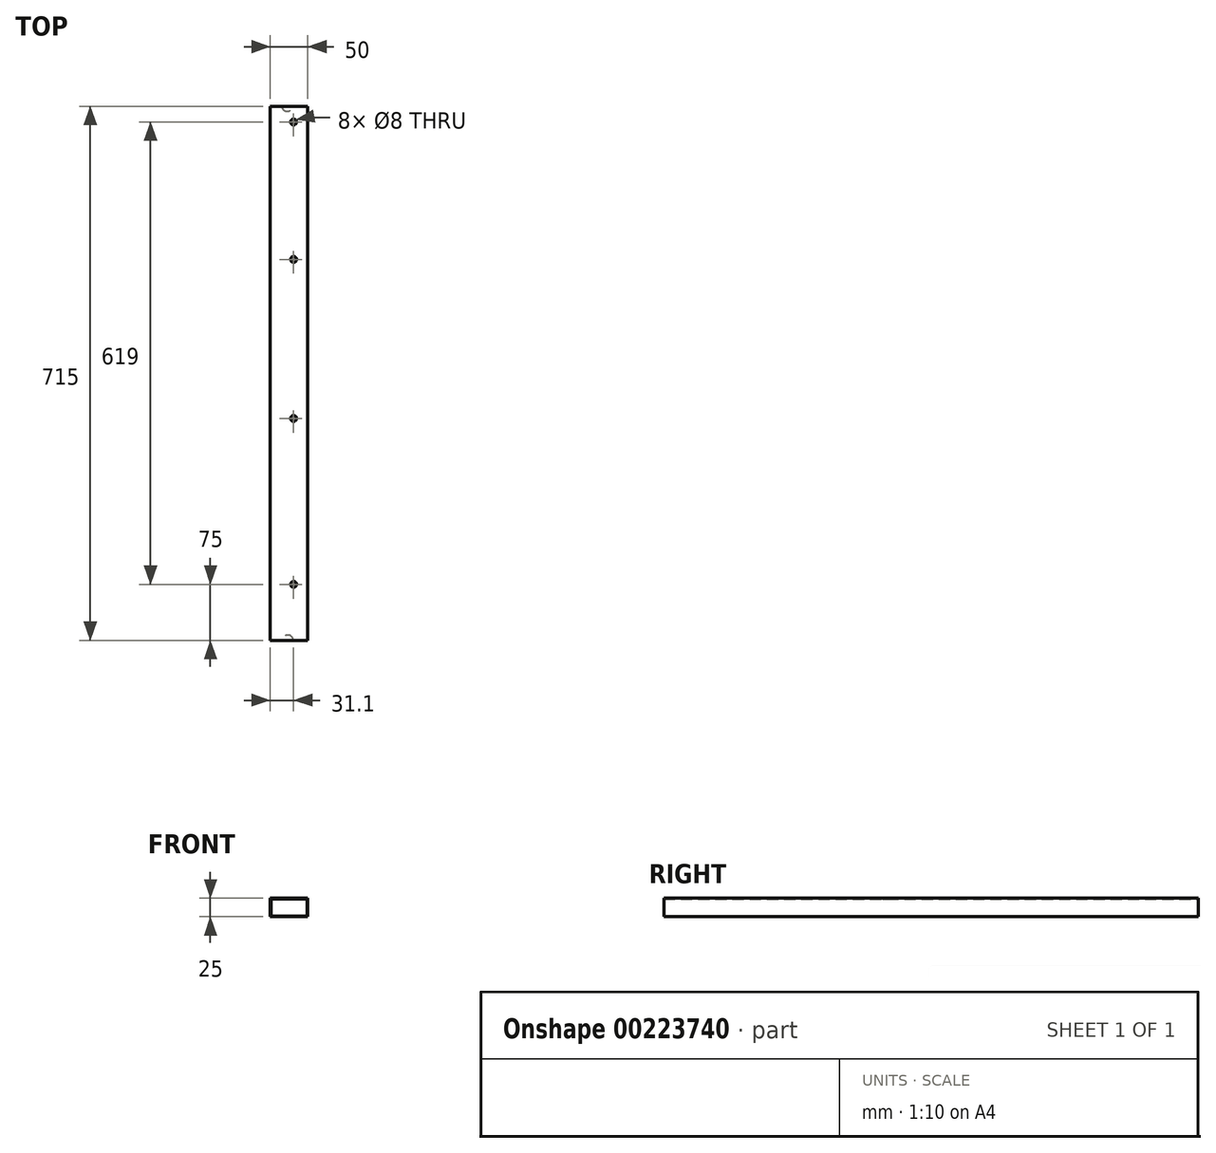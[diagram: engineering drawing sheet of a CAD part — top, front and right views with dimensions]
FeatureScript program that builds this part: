
annotation { "Feature Type Name" : "Feature", "Feature Type Description" : "" }
export const myFeature = defineFeature(function(context is Context, id is Id, definition is map)
    precondition{}
    {
        {
            var Q0;
            Q0=qCreatedBy(makeId("Front.planeOp"),FACE);
            var sketch = newSketch(context, id + "F0", { "sketchPlane" : qUnion([Q0])});
            skLineSegment(sketch, "E0", {"start": v(0, 0) * mm, "end": v(0, 25) * mm});
            skLineSegment(sketch, "E1", {"start": v(1.1, 23.9) * mm, "end": v(1.1, 0.9) * mm});
            skLineSegment(sketch, "E2", {"start": v(1.1, 0.9) * mm, "end": v(49.1, 0.9) * mm});
            skLineSegment(sketch, "E3", {"start": v(50, 0) * mm, "end": v(0, 0) * mm});
            skLineSegment(sketch, "E4", {"start": v(1.1, 23.9) * mm, "end": v(49.1, 23.9) * mm});
            skLineSegment(sketch, "E5", {"start": v(49.1, 23.9) * mm, "end": v(49.1, 0.9) * mm});
            skLineSegment(sketch, "E6", {"start": v(0, 25) * mm, "end": v(50, 25) * mm});
            skLineSegment(sketch, "E7", {"start": v(50, 25) * mm, "end": v(50, 0) * mm});
            skSolve(sketch);
        }
        {
            var Q0;
            Q0=qSketchRegion(id+"F0",true);
            extrude(context, id + "F1", {"entities" : qUnion([Q0]), "depth" : 715 * mm});
        }
        {
            var Q0;
            Q0=qCreatedBy(makeId("Top.planeOp"),FACE);
            var sketch = newSketch(context, id + "F2", { "sketchPlane" : qUnion([Q0])});
            skPoint(sketch, "E8", {"position": v(31.1, -21) * mm});
            skPoint(sketch, "E9", {"position": v(31.1, -205) * mm});
            skPoint(sketch, "E10", {"position": v(31.1, -418) * mm});
            skPoint(sketch, "E11", {"position": v(31.1, -640) * mm});
            skCircle(sketch, "E12", {"center": v(23.16, -2.16) * mm, "radius": 5.5 * mm});
            skSolve(sketch);
        }
        {
            var Q0;
            Q0=sQuery(id+"F2.wireOp",VERTEX,"E8");
            var Q1;
            Q1=sQuery(id+"F2.wireOp",VERTEX,"E9");
            var Q2;
            Q2=sQuery(id+"F2.wireOp",VERTEX,"E10");
            var Q3;
            Q3=sQuery(id+"F2.wireOp",VERTEX,"E11");
            var Q4;
            Q4=makeQuery(id+"F1.opExtrude","SWEPT_BODY",BODY,{"disambiguationData":[OSD([sQuery(id+"F0.wireOp",EDGE,"E0"),sQuery(id+"F0.wireOp",EDGE,"duvrUNqz-dqKf-yXlG-KKZS-6Oz7JXU3pn3h"),sQuery(id+"F0.wireOp",EDGE,"E1"),sQuery(id+"F0.wireOp",EDGE,"E2"),sQuery(id+"F0.wireOp",EDGE,"5OdA4DjD-90Ye-fS3V-So4A-81FMT4XGCEwy"),sQuery(id+"F0.wireOp",EDGE,"E3")])]});
            hole(context, id + "F3", {"style" : HoleStyle.SIMPLE, "endStyle" : HoleEndStyle.THROUGH, "oppositeDirection" : true, "holeDiameter" : 8 * mm, "startFromSketch" : true, "locations" : qUnion([Q0, Q1, Q2, Q3]), "scope" : qUnion([Q4]), "isTappedThrough" : true});
        }
        {
            var Q0;
            Q0=makeQuery(id+"F1.opExtrude","SWEPT_FACE",FACE,{"disambiguationData":[OSD([sQuery(id+"F0.wireOp",EDGE,"E3")])]});
            cPlane(context, id + "F4", {"entities" : qUnion([Q0]), "cplaneType" : CPlaneType.OFFSET, "offset" : 0 * mm, "width" : 150 * mm, "height" : 150 * mm});
        }
        {
            var Q0;
            Q0=qCreatedBy(id+"F4.planeOp",FACE);
            var sketch = newSketch(context, id + "F5", { "sketchPlane" : qUnion([Q0])});
            skCircle(sketch, "E13", {"center": v(22.44, 0) * mm, "radius": 6.83 * mm});
            skSolve(sketch);
        }
        {
            var Q0;
            Q0=qSketchRegion(id+"F5",true);
            extrude(context, id + "F6", {"entities" : qUnion([Q0]), "operationType" : NewBodyOperationType.REMOVE, "oppositeDirection" : true, "depth" : 5 * mm});
        }
        {
            var Q0;
            Q0=qCreatedBy(id+"F4.planeOp",FACE);
            var sketch = newSketch(context, id + "F7", { "sketchPlane" : qUnion([Q0])});
            skCircle(sketch, "E14", {"center": v(23.4, 715) * mm, "radius": 7.1 * mm});
            skSolve(sketch);
        }
        {
            var Q0;
            Q0=qSketchRegion(id+"F7",true);
            extrude(context, id + "F8", {"entities" : qUnion([Q0]), "operationType" : NewBodyOperationType.REMOVE, "oppositeDirection" : true, "depth" : 5 * mm});
        }
    });
